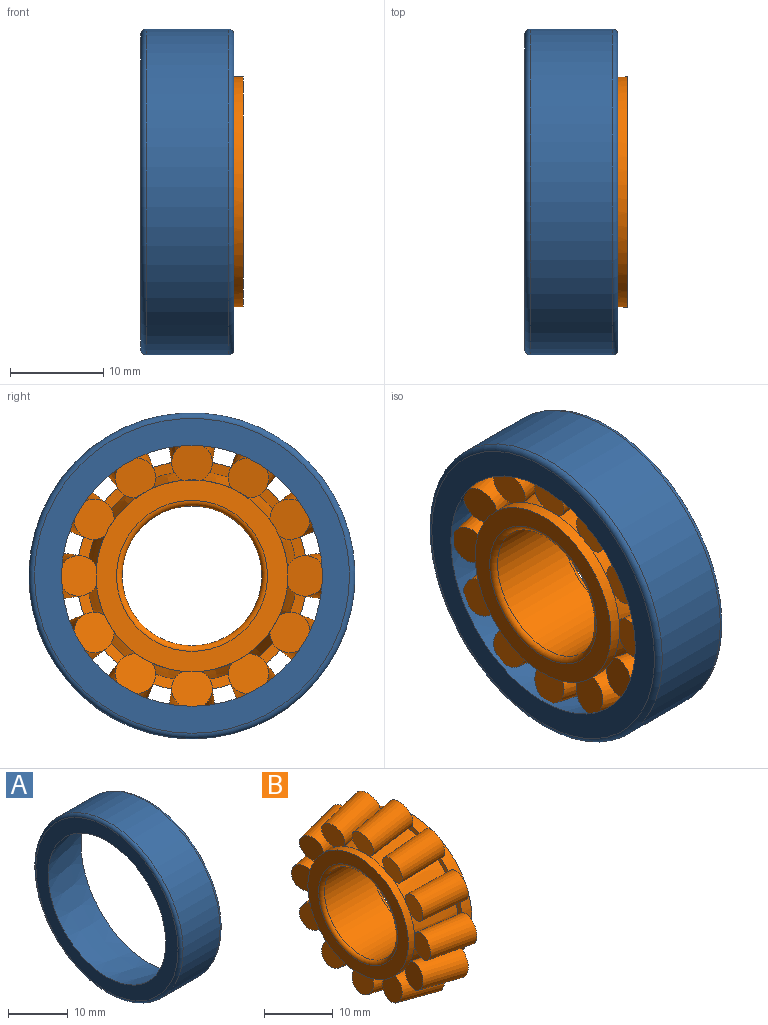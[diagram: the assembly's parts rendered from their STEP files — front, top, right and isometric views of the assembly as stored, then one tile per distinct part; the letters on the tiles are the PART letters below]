
ASSEMBLY  parts=2 mates=1
PART A: 6 faces, bbox 10x37.9x37.9 mm
  f0: torus R=16.9mm, axis (1,0,0), area 102.3mm2, adj f1,f5
  f1: plane 33.8x33.8mm, normal (-1,0,0), area 281.5mm2, adj f0,f2
  f2: cone r=14mm half-angle=12deg, axis (1,0,0), area 967.6mm2, adj f1,f3
  f3: plane 33.8x33.8mm, normal (1,0,0), area 80.4mm2, adj f2,f4
  f4: torus R=16.9mm, axis (1,0,0), area 102.3mm2, adj f3,f5
  f5: cylinder r=17.5mm len=35mm, axis (1,0,0), area 967.6mm2, adj f0,f4
PART B: 46 faces, bbox 11x31.9x31.9 mm
  f0: cylinder r=12.35mm len=24.7mm, axis (1,0,0), area 151.2mm2, adj f1,f7,f11,f12,f14,f15,f17,f18
  f1: cone r=11.24mm half-angle=79.5deg, axis (-1,0,0), area 47.8mm2, adj f0,f9,f11,f14,f17,f20,f23,f26
  f2: cylinder r=10.3mm len=20.6mm, axis (1,0,0), area 84.6mm2, adj f3,f8
  f3: plane 20.6x20.6mm, normal (-1,0,0), area 127.2mm2, adj f2,f4
  f4: torus R=8.1mm, axis (1,0,0), area 45.7mm2, adj f3,f5
  f5: cylinder r=7.5mm len=15mm, axis (1,0,0), area 461.8mm2, adj f4,f6
  f6: torus R=8.1mm, axis (1,0,0), area 45.7mm2, adj f5,f7
  f7: plane 24.7x24.7mm, normal (1,0,0), area 273mm2, adj f0,f6
  f8: cone r=14.28mm half-angle=79.5deg, axis (-1,0,0), area 20.1mm2, adj f2,f9
  f9: cone r=9.99mm half-angle=9deg, axis (1,0,0), area 532.5mm2, adj f1,f8
  f10: plane 4.35x4.28mm, normal (-0.98,-0.18,0), area 14.9mm2, adj f11
  f11: cone r=2.18mm half-angle=1.5deg, axis (0.98,0.18,0), area 114.4mm2, adj f0,f1,f10,f12
  f12: plane 4.77x3.74mm, normal (0.98,0.18,0), area 14.9mm2, adj f0,f11
  f13: plane 4.34x4.3mm, normal (-0.98,-0.16,-0.09), area 14.9mm2, adj f14
  f14: cone r=2.18mm half-angle=1.5deg, axis (0.98,0.16,0.09), area 114.4mm2, adj f0,f1,f13,f15
  f15: plane 4.75x4.52mm, normal (0.98,0.16,0.09), area 14.9mm2, adj f0,f14
  f16: plane 4.34x4.3mm, normal (-0.98,-0.09,-0.16), area 14.9mm2, adj f17
  f17: cone r=2.18mm half-angle=1.5deg, axis (0.98,0.09,0.16), area 114.4mm2, adj f0,f1,f16,f18
  f18: plane 4.75x4.52mm, normal (0.98,0.09,0.16), area 14.9mm2, adj f0,f17
  f19: plane 4.35x4.28mm, normal (-0.98,0,-0.18), area 14.9mm2, adj f20
  f20: cone r=2.18mm half-angle=1.5deg, axis (0.98,0,0.18), area 114.4mm2, adj f0,f1,f19,f21
  f21: plane 4.77x3.74mm, normal (0.98,0,0.18), area 14.9mm2, adj f0,f20
  f22: plane 4.34x4.3mm, normal (-0.98,0.09,-0.16), area 14.9mm2, adj f23
  f23: cone r=2.18mm half-angle=1.5deg, axis (0.98,-0.09,0.16), area 114.4mm2, adj f0,f1,f22,f24
  f24: plane 4.75x4.52mm, normal (0.98,-0.09,0.16), area 14.9mm2, adj f0,f23
  f25: plane 4.34x4.3mm, normal (-0.98,0.16,-0.09), area 14.9mm2, adj f26
  f26: cone r=2.18mm half-angle=1.5deg, axis (0.98,-0.16,0.09), area 114.4mm2, adj f0,f1,f25,f27
  f27: plane 4.75x4.52mm, normal (0.98,-0.16,0.09), area 14.9mm2, adj f0,f26
  f28: plane 4.35x4.28mm, normal (-0.98,0.18,0), area 14.9mm2, adj f29
  f29: cone r=2.18mm half-angle=1.5deg, axis (0.98,-0.18,0), area 114.4mm2, adj f0,f1,f28,f30
  f30: plane 4.77x3.74mm, normal (0.98,-0.18,0), area 14.9mm2, adj f0,f29
  f31: plane 4.34x4.3mm, normal (-0.98,0.16,0.09), area 14.9mm2, adj f32
  f32: cone r=2.18mm half-angle=1.5deg, axis (0.98,-0.16,-0.09), area 114.4mm2, adj f0,f1,f31,f33
  f33: plane 4.75x4.52mm, normal (0.98,-0.16,-0.09), area 14.9mm2, adj f0,f32
  f34: plane 4.34x4.3mm, normal (-0.98,0.09,0.16), area 14.9mm2, adj f35
  f35: cone r=2.18mm half-angle=1.5deg, axis (0.98,-0.09,-0.16), area 114.4mm2, adj f0,f1,f34,f36
  f36: plane 4.75x4.52mm, normal (0.98,-0.09,-0.16), area 14.9mm2, adj f0,f35
  f37: plane 4.35x4.28mm, normal (-0.98,0,0.18), area 14.9mm2, adj f38
  f38: cone r=2.18mm half-angle=1.5deg, axis (0.98,0,-0.18), area 114.4mm2, adj f0,f1,f37,f39
  f39: plane 4.79x3.75mm, normal (0.98,0,-0.18), area 14.9mm2, adj f0,f38
  f40: plane 4.34x4.3mm, normal (-0.98,-0.09,0.16), area 14.9mm2, adj f41
  f41: cone r=2.18mm half-angle=1.5deg, axis (0.98,0.09,-0.16), area 114.4mm2, adj f0,f1,f40,f42
  f42: plane 4.75x4.52mm, normal (0.98,0.09,-0.16), area 14.9mm2, adj f0,f41
  f43: plane 4.34x4.3mm, normal (-0.98,-0.16,0.09), area 14.9mm2, adj f44
  f44: cone r=2.18mm half-angle=1.5deg, axis (0.98,0.16,-0.09), area 114.4mm2, adj f0,f1,f43,f45
  f45: plane 4.75x4.52mm, normal (0.98,0.16,-0.09), area 14.9mm2, adj f0,f44
PLACE A t=(0.75,0,0)mm
PLACE B at identity
MATE fastened A.f0 <-> B.f0  axis (-1,0,0) through (-11,0,0)mm
